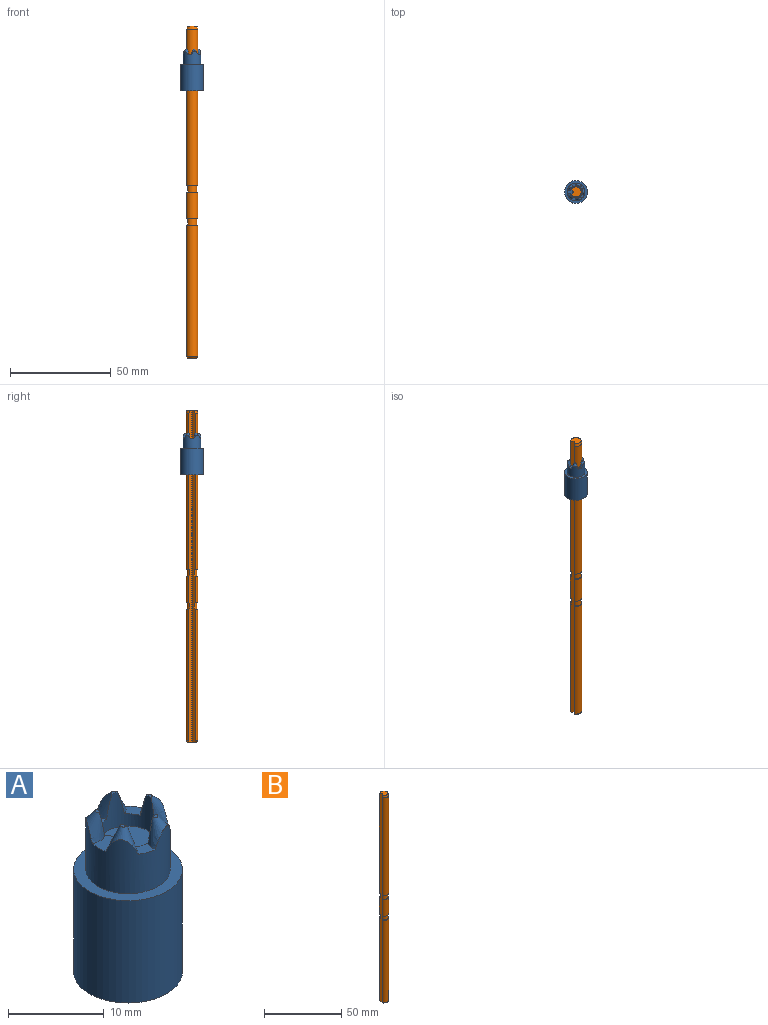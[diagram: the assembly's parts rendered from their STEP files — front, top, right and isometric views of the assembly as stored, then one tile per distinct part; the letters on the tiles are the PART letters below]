
ASSEMBLY  parts=2 mates=1
PART A: 33 faces, bbox 11.7x11.7x21.3 mm
  f0: cylinder r=3.06mm len=6.12mm, axis (0,0,-1), area 44.5mm2, adj f1,f4,f6,f7,f10,f11,f12,f13
  f1: cylinder r=0.15mm len=4.37mm, axis (0,0,-1), area 0.8mm2, adj f0,f2,f17,f32
  f2: plane 3.77x0.68mm, normal (0.71,0.71,0), area 1.9mm2, adj f1,f5,f17,f18,f32
  f3: plane 3.77x0.68mm, normal (0.71,-0.71,0), area 1.9mm2, adj f4,f5,f18,f22,f32
  f4: cylinder r=0.15mm len=4.37mm, axis (0,0,-1), area 0.8mm2, adj f0,f3,f22,f32
  f5: cylinder r=0.9mm len=1.57mm, axis (0,0,-1), area 2.2mm2, adj f2,f3,f18,f32
  f6: cone r=1.8mm half-angle=24.8deg, axis (0.34,0,-0.94), area 9mm2, adj f0,f7,f9,f10,f27
  f7: plane 0.97x0.71mm, normal (0,0,1), area 0.2mm2, adj f0,f6
  f8: cylinder r=3.06mm len=15.9mm, axis (0,0,-1), area 255.9mm2, adj f15,f21,f29,f31
  f9: cylinder r=4.4mm len=8.8mm, axis (0,0,-1), area 159.2mm2, adj f6,f10,f12,f13,f17,f18,f22,f23
  f10: plane 2.32x2.22mm, normal (0,0,1), area 2.2mm2, adj f0,f6,f9,f12
  f11: plane 0.97x0.81mm, normal (0,0,1), area 0.2mm2, adj f0,f12
  f12: cone r=1.8mm half-angle=24.8deg, axis (0.11,0.33,-0.94), area 9mm2, adj f0,f9,f10,f11,f13
  f13: plane 2.2x1.91mm, normal (0,0,1), area 2.2mm2, adj f0,f9,f12,f17
  f14: plane 0.63x0.58mm, normal (0,0,1), area 0.2mm2, adj f0,f17
  f15: cylinder r=0.15mm len=15.9mm, axis (0,0,-1), area 3.1mm2, adj f8,f16,f29,f31
  f16: plane 15.9x0.68mm, normal (0.71,0.71,0), area 15.3mm2, adj f15,f26,f29,f31
  f17: cone r=1.8mm half-angle=24.8deg, axis (-0.28,0.2,-0.94), area 9.8mm2, adj f0,f1,f2,f9,f13,f14,f18
  f18: plane 2.7x2.17mm, normal (0,0,1), area 4.4mm2, adj f2,f3,f5,f9,f17,f22
  f19: plane 0.63x0.58mm, normal (0,0,1), area 0.2mm2, adj f0,f22
  f20: plane 15.9x0.68mm, normal (0.71,-0.71,0), area 15.3mm2, adj f21,f26,f29,f31
  f21: cylinder r=0.15mm len=15.9mm, axis (0,0,-1), area 3.1mm2, adj f8,f20,f29,f31
  f22: cone r=1.8mm half-angle=24.8deg, axis (-0.28,-0.2,-0.94), area 9.8mm2, adj f0,f3,f4,f9,f18,f19,f23
  f23: plane 2.2x1.91mm, normal (0,0,1), area 2.2mm2, adj f0,f9,f22,f24
  f24: cone r=1.8mm half-angle=24.8deg, axis (0.11,-0.33,-0.94), area 9mm2, adj f0,f9,f23,f25,f27
  f25: plane 0.97x0.81mm, normal (0,0,1), area 0.2mm2, adj f0,f24
  f26: cylinder r=0.9mm len=15.9mm, axis (0,0,-1), area 22.5mm2, adj f16,f20,f29,f31
  f27: plane 2.32x2.22mm, normal (0,0,1), area 2.2mm2, adj f0,f6,f9,f24
  f28: cylinder r=5.68mm len=13.05mm, axis (0,0,1), area 465.3mm2, adj f29,f30
  f29: plane 11.35x11.35mm, normal (0,0,-1), area 74.2mm2, adj f8,f15,f16,f20,f21,f26,f28
  f30: plane 11.35x11.35mm, normal (0,0,1), area 40.4mm2, adj f9,f28
  f31: plane 6.12x5.75mm, normal (0,0,-1), area 27mm2, adj f8,f15,f16,f20,f21,f26
  f32: plane 6.12x5.75mm, normal (0,0,1), area 27mm2, adj f0,f1,f2,f3,f4,f5
PART B: 16 faces, bbox 5.6x5.9x165 mm
  f0: cylinder r=2.95mm len=13.2mm, axis (0,0,-1), area 201.2mm2, adj f2,f4,f11,f15
  f1: cylinder r=2.95mm len=65.4mm, axis (0,0,-1), area 996.7mm2, adj f2,f4,f8,f12
  f2: plane 165.02x1.36mm, normal (-0.71,0.71,0), area 307.8mm2, adj f0,f1,f3,f5,f6,f7,f8,f9
  f3: cylinder r=2.95mm len=77.7mm, axis (0,0,-1), area 1184.2mm2, adj f2,f4,f9,f14
  f4: plane 165.02x1.36mm, normal (-0.71,-0.71,0), area 307.8mm2, adj f0,f1,f3,f5,f6,f7,f8,f9
  f5: cylinder r=0.3mm len=165mm, axis (0,0,-1), area 77.8mm2, adj f2,f4,f6,f7
  f6: plane 5.09x4.75mm, normal (0,0,1), area 18.2mm2, adj f2,f4,f5,f9
  f7: plane 4.69x4.41mm, normal (0,0,-1), area 15.6mm2, adj f2,f4,f5,f8
  f8: cone r=2.95mm half-angle=45deg, axis (0,0,1), area 11.7mm2, adj f1,f2,f4,f7
  f9: cone r=2.54mm half-angle=15deg, axis (0,0,-1), area 22.2mm2, adj f2,f3,f4,f6
  f10: cylinder r=2.4mm len=4.8mm, axis (0,0,-1), area 41.8mm2, adj f2,f4,f11,f12
  f11: plane 5.89x5.45mm, normal (0,0,-1), area 7.6mm2, adj f0,f2,f4,f10
  f12: plane 5.89x5.45mm, normal (0,0,1), area 7.6mm2, adj f1,f2,f4,f10
  f13: cylinder r=2.4mm len=4.8mm, axis (0,0,-1), area 41.8mm2, adj f2,f4,f14,f15
  f14: plane 5.89x5.45mm, normal (0,0,-1), area 7.6mm2, adj f2,f3,f4,f13
  f15: plane 5.89x5.45mm, normal (0,0,1), area 7.6mm2, adj f0,f2,f4,f13
PLACE A at identity fixed
PLACE B t=(0,0,-145.75)mm
MATE fastened B.f0 <-> A.f0  axis (0,0,1) through (0,0,19.25)mm
